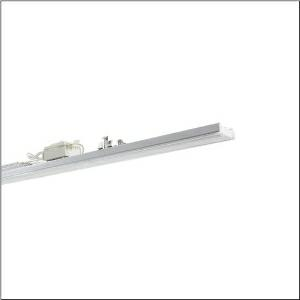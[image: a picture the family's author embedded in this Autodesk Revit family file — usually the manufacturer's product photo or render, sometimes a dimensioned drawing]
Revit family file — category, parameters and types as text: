
# Revit family: licross_r__11_recessed_mo_51tl12dn4axgd_4589
name_source: partatom
category: Lighting Fixtures
units: mm (PartAtom-declared; Revit-internal decimal feet)

## family parameters
Cut with Voids When Loaded = No
Host = Face
Light Source = No
Part Type = Normal
Room Calculation Point = No
Round Connector Dimension = Use Diameter
Shared = No

## types (1)
- --- (1 x LED, 1540 lm, 9.2 W, 4000K)
    Apparent Load = 9 VA
    CIE Flux Codes = 67 92 99 100 100
    Color Rendering = 80
    Color Temperature = 4000K
    Default Elevation = 1800 mm
    Description = Licross® 11 Recessed MO, luminaire insert, of sheet steel, coil coated, white, length: 1.500mm, width: 66mm, height: 67mm, LED rated luminous flux: 10.240lm, light colour: 840, control gear: DALI 2 (for two DALI lines), with plug, 6-pole, with phase selection, mains connection: 220..240V, AC/DC, 0/50..60Hz, rated input power: 57W, without changeover relay, for emergency light function, for central battery installations according to DIN EN 60598-2-22, halogen-free wiring, primary optical cover: cover, of PMMA, light emission: direct distribution, primary light characteristic: symmetric, protection rating (complete): IP40, insulation class (complete): insulation class I (protective earthing), certification: CE, ENEC, VDE, UKCA, protection symbol: D if used in an environment without relevant dust loads with corresponding accessories, impact resistance: IK06, permissible ambient temperature for indoor applications: -25..+35°C, standard: EN 60598-2-22, corresponds to IFS (International Featured Standards) requirements for safety and quality in the food industry, reducing of maximum allowable ambient temperature of 5°C with ceiling mounting, LABS conformity tested according to VDMA 24364:2018-05, packaging unit: 1 piece
    Height = 58 mm
    Lamp = 1 x LED
    Lamp Light Flux = 1540 lm
    Lamp Power = 9.2 W
    Lamp count = 1
    Length = 1500 mm
    Luminous efficacy = 167 lm/W
    Manufacturer = Siteco
    ModVariant = No
    Model = 51TL12DN4AXGD
    Mounting Place = Ceiling
    Mounting Type = Pendant
    Number of Poles = 1
    OnlyDefault = Yes
    Power Factor = 1
    Product Name = Licross® 11 Recessed MO
    Product group = luminaire insert
    ProductGroupID = 902
    Protection Class = Protection class I
    Protection Degree = IP 40
    RLX_Detail_Level = 1
    RLX_Emergency_Light_Flux = 0 lm
    RLX_Emergency_Type = 0
    RLX_Emergency_Type_DB = No
    RlxData = <blob elided: 24821 chars, md5=aa4e3bd4>
    Socket = socket
    Standby Power = 0 W
    System Light Flux = 1540 lm
    System Power = 9 W
    Type Comments = : DC mode (central or group accumulator) initial emergency light level
    Type Image = l_1296930.jpg
    URL = http://relux.com
    VarID = @adj_087472
    Voltage = 0 V
    Weight = 0.00 kg
    Width = 66 mm

## geometry (parser evidence)
native form markers: Blend x4, Sweep x12
no freeform markers — native parametric forms only
